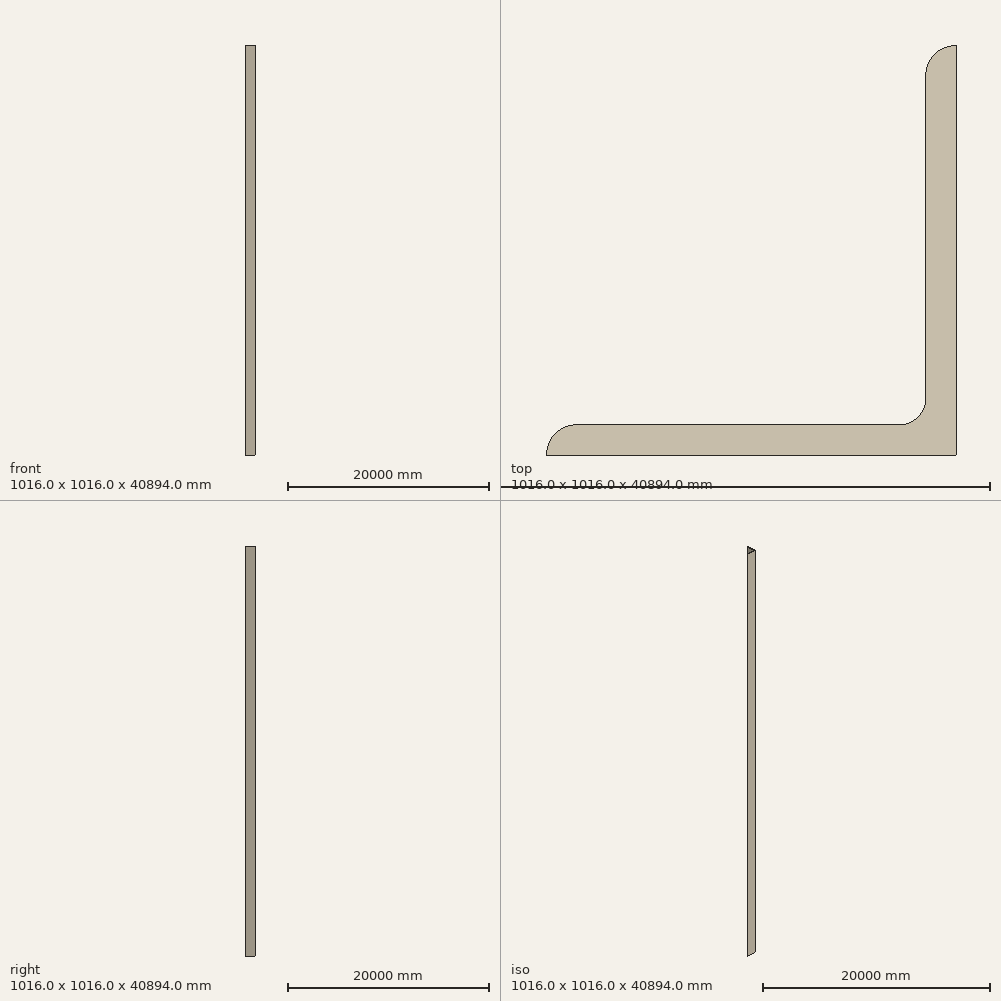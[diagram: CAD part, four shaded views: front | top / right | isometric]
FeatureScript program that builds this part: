
annotation { "Feature Type Name" : "Feature", "Feature Type Description" : "" }
export const myFeature = defineFeature(function(context is Context, id is Id, definition is map)
    precondition{}
    {
        {
            var Q0;
            Q0=qCreatedBy(makeId("Top.planeOp"),FACE);
            var sketch = newSketch(context, id + "F0", { "sketchPlane" : qUnion([Q0])});
            skLineSegment(sketch, "E0", {"start": v(0, 0) * mm, "end": v(1016, 0) * mm});
            skLineSegment(sketch, "E1", {"start": v(1016, 0) * mm, "end": v(1016, 1016) * mm});
            skLineSegment(sketch, "E2", {"start": v(939.8, 939.8) * mm, "end": v(939.8, 139.7) * mm});
            skLineSegment(sketch, "E3", {"start": v(876.3, 76.2) * mm, "end": v(76.2, 76.2) * mm});
            skArc(sketch, "E4", {"start": v(939.8, 939.8) * mm, "mid": v(962.12, 993.68) * mm, "end": v(1016, 1016) * mm});
            skArc(sketch, "E5", {"start": v(0, 0) * mm, "mid": v(22.32, 53.88) * mm, "end": v(76.2, 76.2) * mm});
            skPoint(sketch, "E6.visualSharp", {"position": v(939.8, 76.2) * mm});
            skArc(sketch, "E6.filletArc", {"start": v(876.3, 76.2) * mm, "mid": v(921.2, 94.8) * mm, "end": v(939.8, 139.7) * mm});
            skSolve(sketch);
        }
        {
            var Q0;
            Q0=makeQuery(id+"F0.imprint","IMPRINT",FACE,{"disambiguationData":[TD([[makeQuery(id+"F0.imprint","IMPRINT",EDGE,{"derivedFrom":sQuery(id+"F0.wireOp",EDGE,"E0")}),1.0]])]});
            extrude(context, id + "F1", {"entities" : qUnion([Q0]), "depth" : 40894 * mm, "offsetDistance" : 25.4 * mm});
        }
    });
